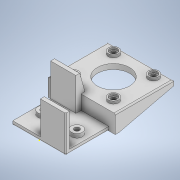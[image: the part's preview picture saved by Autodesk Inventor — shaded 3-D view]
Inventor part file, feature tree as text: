
AUTODESK INVENTOR PART (.ipt)
format: ipt  version: 2020 (Build 240168000, 168)  size: 375,808 bytes
history: native  units: in
note: dims shown in document units (in); Inventor stores cm internally (conversion verified against a paired STEP export)
features: sketch x20, extrude x19, fillet x1
ambient origin geometry x8: Origin, YZ Plane, XZ Plane, XY Plane, X Axis, Y Axis, Z Axis, Center Point
bodies: Solid1 (feature_tree)
feature tree (40):
  extrude  "Extrusion1"  Depth=1.2756in
  extrude  "Extrusion3"  Depth=0.1181in
  extrude  "Extrusion4"  Depth=1.0in TaperAngle=0.0deg
  extrude  "Extrusion5"  Depth=0.1181in TaperAngle=0.0deg
  extrude  "Extrusion6"  Depth=0.1181in TaperAngle=0.0deg
  extrude  "Extrusion7"  Depth=0.3346in
  extrude  "Extrusion8"  Depth=0.1575in
  sketch  "Sketch14"  dims[d25=0.1575in d26=0.2362in d27=0.0in]
  extrude  "Extrusion14"  Depth=0.2362in TaperAngle=0.0deg
  extrude  "Extrusion15"  Depth=0.2362in
  extrude  "Extrusion16"  Depth=0.1181in
  extrude  "Extrusion17"  Depth=0.2953in
  extrude  "Extrusion18"  Depth=0.1575in
  extrude  "Extrusion19"  Depth=0.1575in TaperAngle=0.0deg
  extrude  "Extrusion20"  Depth=1.6654in TaperAngle=0.0deg
  extrude  "Extrusion21"  Depth=0.315in
  extrude  "Extrusion22"  Depth=0.315in
  extrude  "Extrusion23"  Depth=0.0787in
  extrude  "Extrusion24"  Depth=0.1575in
  extrude  "Extrusion25"  Depth=0.1575in
  fillet  "Fillet2"  Radius=0.3937in
  sketch  "Sketch1"  dims[d0=1.6142in d1=1.2756in]
  sketch  "Sketch3"  dims[d2=0.1181in d3=0.0in d8=0.1181in]
  sketch  "Sketch4"  dims[d9=0.1181in d10=1.0in d11=0.0in]
  sketch  "Sketch5"  dims[d12=0.8465in d13=0.1181in d14=0.0in]
  sketch  "Sketch6"  dims[d15=0.8465in d16=0.1181in d17=0.0in]
  sketch  "Sketch7"  dims[d20=0.3346in d21=0.3346in]
  sketch  "Sketch8"  dims[d22=0.1181in d23=0.0in d24=0.1575in]
  sketch  "Sketch15"  dims[d28=0.2362in d29=0.2362in]
  sketch  "Sketch16"  dims[d30=0.1181in d31=0.0in d54=0.2953in]
  sketch  "Sketch17"  dims[d65=1.0236in d66=0.2953in]
  sketch  "Sketch18"  dims[d67=0.5512in d68=0.1575in]
  sketch  "Sketch19"  dims[d69=0.1575in d70=0.1575in d71=0.0in]
  sketch  "Sketch20"  dims[d72=0.1575in d73=1.6654in d74=0.0in]
  sketch  "Sketch21"  dims[d76=0.315in d77=0.315in]
  sketch  "Sketch22"  dims[d78=0.315in d79=0.315in]
  sketch  "Sketch23"  dims[d80=0.0787in d81=0.0in d82=0.9843in]
  sketch  "Sketch24"  dims[d83=0.1575in d84=0.1575in]
  sketch  "Sketch25"  dims[d85=0.1575in d86=0.1575in d87=0.3937in d88=0.0in]
  sketch  "Sketch26"  dims[d89=0.2362in d90=0.2362in d91=0.2362in d92=0.2362in d93=0.0591in d94=0.0in d95=0.1969in d96=0.0in d97=0.1969in d98=0.0in d99=0.1575in d100=0.1575in d101=0.3937in d102=0.0in d103=2.3622in d104=0.0in d105=2.3622in d106=0.0in d107=0.0394in d108=1.0433in d109=0.0in d110=0.0394in d111=0.1969in d112=0.0in d113=0.0394in d62=0.0197in d63=0.0344in d64=0.0197in]
